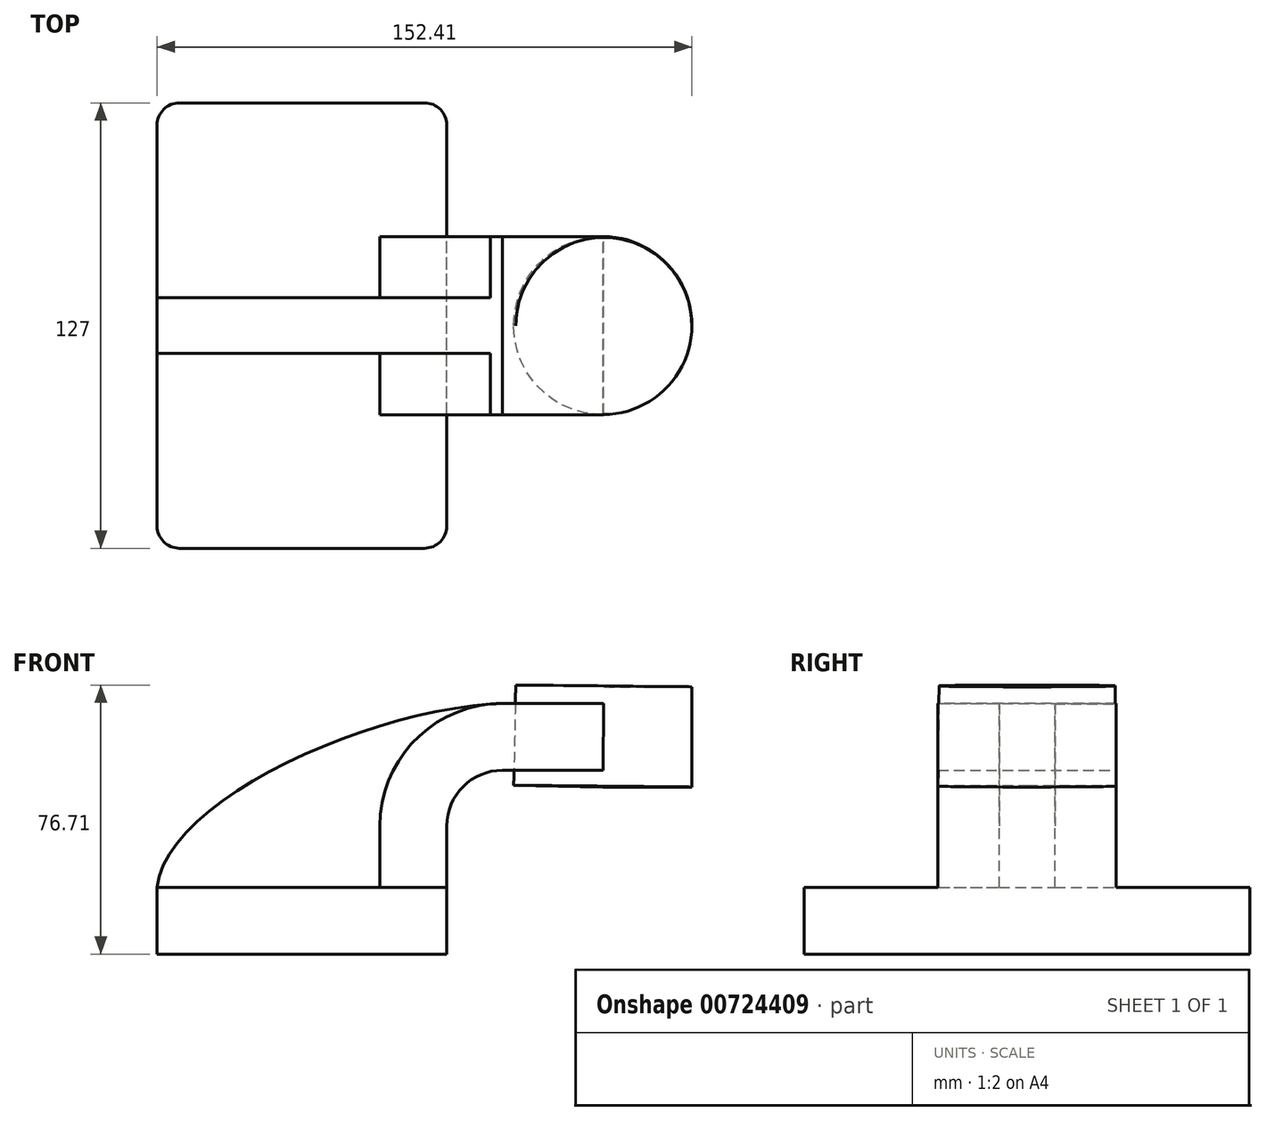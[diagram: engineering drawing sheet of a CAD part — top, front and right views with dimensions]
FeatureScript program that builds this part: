
annotation { "Feature Type Name" : "Feature", "Feature Type Description" : "" }
export const myFeature = defineFeature(function(context is Context, id is Id, definition is map)
    precondition{}
    {
        {
            var Q0;
            Q0=qCreatedBy(makeId("Front.planeOp"),FACE);
            var sketch = newSketch(context, id + "F0", { "sketchPlane" : qUnion([Q0])});
            skLineSegment(sketch, "E0.bottom", {"start": v(-41.27, -9.53) * mm, "end": v(41.28, -9.53) * mm});
            skLineSegment(sketch, "E0.top", {"start": v(-41.28, 9.53) * mm, "end": v(41.28, 9.53) * mm});
            skLineSegment(sketch, "E0.left", {"start": v(-41.28, -9.52) * mm, "end": v(-41.28, 9.53) * mm});
            skLineSegment(sketch, "E0.right", {"start": v(41.28, -9.53) * mm, "end": v(41.28, 9.53) * mm});
            skPoint(sketch, "E0.middle", {"position": v(0, 0) * mm});
            skLineSegment(sketch, "E1.bottom", {"start": v(60.32, 38.1) * mm, "end": v(111.12, 38.1) * mm});
            skLineSegment(sketch, "E1.top", {"start": v(60.32, 66.68) * mm, "end": v(111.12, 66.68) * mm});
            skLineSegment(sketch, "E1.left", {"start": v(60.32, 38.1) * mm, "end": v(60.32, 66.68) * mm});
            skLineSegment(sketch, "E1.right", {"start": v(111.12, 38.1) * mm, "end": v(111.12, 66.68) * mm});
            skPoint(sketch, "E1.middle", {"position": v(85.72, 52.39) * mm});
            skLineSegment(sketch, "E2", {"start": v(41.27, 9.53) * mm, "end": v(41.27, 27) * mm});
            skArc(sketch, "E3", {"start": v(41.27, 27) * mm, "mid": v(45.92, 38.23) * mm, "end": v(57.15, 42.88) * mm});
            skLineSegment(sketch, "E4", {"start": v(57.15, 42.88) * mm, "end": v(86.01, 42.88) * mm});
            skLineSegment(sketch, "E5.0", {"start": v(57.15, 61.93) * mm, "end": v(86.01, 61.93) * mm});
            skArc(sketch, "E5.1", {"start": v(22.22, 27) * mm, "mid": v(32.45, 51.7) * mm, "end": v(57.15, 61.93) * mm});
            skLineSegment(sketch, "E5.2", {"start": v(22.22, 9.53) * mm, "end": v(22.22, 27) * mm});
            skLineSegment(sketch, "E6", {"start": v(85.72, 38.1) * mm, "end": v(86.01, 66.68) * mm});
            skFitSpline(sketch, "E7", {"points": [v(-41.28, 9.53) * mm, v(57.15, 61.93) * mm], "startDerivative": vector(7.51, 74.57) * mm, "endDerivative": vector(111.87, 3.34) * mm});
            skSolve(sketch);
        }
        {
            var Q0;
            Q0=makeQuery(id+"F0.imprint","IMPRINT",FACE,{"disambiguationData":[TD([[makeQuery(id+"F0.imprint","IMPRINT",EDGE,{"derivedFrom":sQuery(id+"F0.wireOp",EDGE,"E0.bottom")}),1.0]])]});
            extrude(context, id + "F1", {"entities" : qUnion([Q0]), "endBound" : BoundingType.SYMMETRIC, "depth" : 127 * mm, "offsetDistance" : 25.4 * mm});
        }
        {
            var Q0;
            {var subQ1=sQuery(id+"F0.wireOp",EDGE,"E2");Q0=makeQuery(id+"F0.imprint","IMPRINT",FACE,{"disambiguationData":[TD([[makeQuery(id+"F0.imprint","IMPRINT",EDGE,{"derivedFrom":subQ1}),1.0]])]});}
            var Q1;
            {var subQ0=sQuery(id+"F0.wireOp",EDGE,"E4");var subQ1=sQuery(id+"F0.wireOp",EDGE,"E1.left");var subQ2=makeQuery(id+"F0.imprint","INTERSECT",VERTEX,{"derivedFrom":[subQ1,subQ0]});Q1=makeQuery(id+"F0.imprint","IMPRINT",FACE,{"disambiguationData":[TD([[makeQuery(id+"F0.imprint","IMPRINT",EDGE,{"disambiguationData":[TD([[subQ2,-1.0]])],"derivedFrom":subQ1}),-1.0]])]});}
            extrude(context, id + "F2", {"entities" : qUnion([Q0, Q1]), "operationType" : NewBodyOperationType.ADD, "endBound" : BoundingType.SYMMETRIC, "depth" : 50.8 * mm, "offsetDistance" : 25.4 * mm});
        }
        {
            var Q0;
            {var subQ3=sQuery(id+"F0.wireOp",EDGE,"E5.2");Q0=makeQuery(id+"F0.imprint","IMPRINT",FACE,{"disambiguationData":[TD([[makeQuery(id+"F0.imprint","IMPRINT",EDGE,{"derivedFrom":subQ3}),1.0]])]});}
            extrude(context, id + "F3", {"entities" : qUnion([Q0]), "operationType" : NewBodyOperationType.ADD, "endBound" : BoundingType.SYMMETRIC, "depth" : 15.88 * mm, "offsetDistance" : 25.4 * mm});
        }
        {
            var Q0;
            {var subQ4=sQuery(id+"F0.wireOp",EDGE,"E1.right");Q0=makeQuery(id+"F0.imprint","IMPRINT",FACE,{"disambiguationData":[TD([[makeQuery(id+"F0.imprint","IMPRINT",EDGE,{"derivedFrom":subQ4}),1.0]])]});}
            var Q1;
            Q1=sQuery(id+"F0.wireOp",EDGE,"E6");
            revolve(context, id + "F4", {"surfaceOperationType" : NewSurfaceOperationType.NEW, "entities" : qUnion([Q0]), "axis" : qUnion([Q1]), "revolveType" : RevolveType.FULL});
        }
        {
            var Q0;
            Q0=makeQuery(id+"F1.opExtrude","CAP_EDGE",EDGE,{"disambiguationData":[OSD([sQuery(id+"F0.wireOp",EDGE,"E0.left")])],"isStart":false});
            var Q1;
            Q1=makeQuery(id+"F1.opExtrude","CAP_EDGE",EDGE,{"disambiguationData":[OSD([sQuery(id+"F0.wireOp",EDGE,"E0.right")])],"isStart":false});
            var Q2;
            Q2=makeQuery(id+"F1.opExtrude","CAP_EDGE",EDGE,{"disambiguationData":[OSD([sQuery(id+"F0.wireOp",EDGE,"E0.right")])],"isStart":true});
            var Q3;
            Q3=makeQuery(id+"F1.opExtrude","CAP_EDGE",EDGE,{"disambiguationData":[OSD([sQuery(id+"F0.wireOp",EDGE,"E0.left")])],"isStart":true});
            fillet(context, id + "F5", {"entities" : qUnion([Q0, Q1, Q2, Q3]), "radius" : 6.35 * mm, "tangentPropagation" : true, "allowEdgeOverflow" : false});
        }
    });
